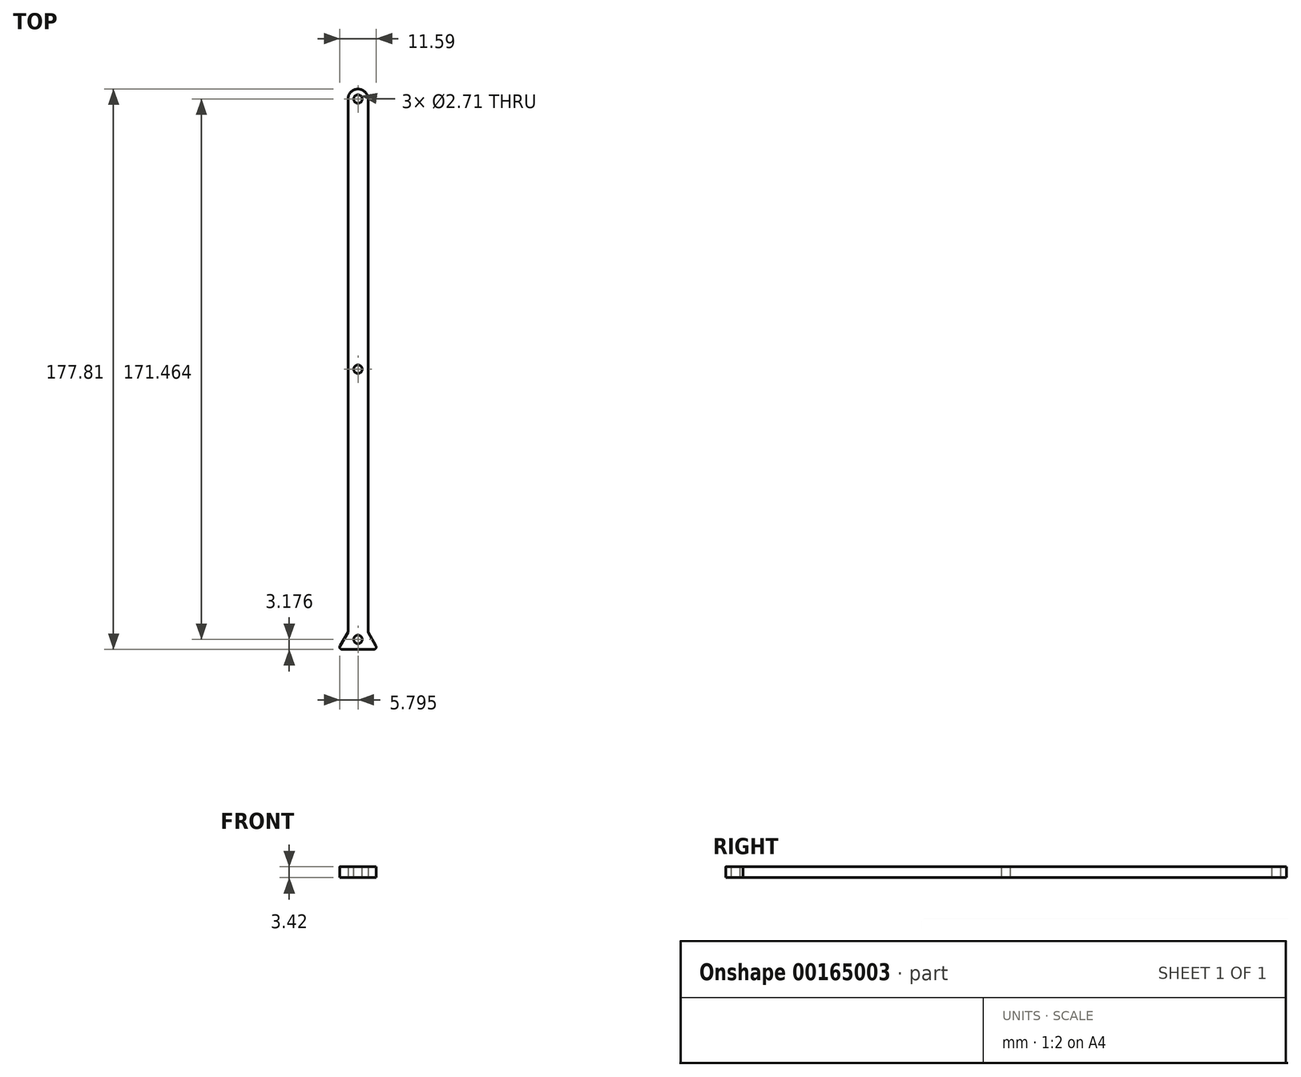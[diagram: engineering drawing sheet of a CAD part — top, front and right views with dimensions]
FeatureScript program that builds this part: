
annotation { "Feature Type Name" : "Feature", "Feature Type Description" : "" }
export const myFeature = defineFeature(function(context is Context, id is Id, definition is map)
    precondition{}
    {
        {
            var Q0;
            Q0=qCreatedBy(makeId("Top.planeOp"),FACE);
            var sketch = newSketch(context, id + "F0", { "sketchPlane" : qUnion([Q0])});
            skLineSegment(sketch, "E0.bottom", {"start": v(0, 0) * mm, "end": v(6.35, 0) * mm, "construction": true});
            skLineSegment(sketch, "E0.top", {"start": v(0, -169.14) * mm, "end": v(6.35, -169.14) * mm, "construction": true});
            skLineSegment(sketch, "E0.left", {"start": v(0, 0) * mm, "end": v(0, -169.14) * mm});
            skLineSegment(sketch, "E0.right", {"start": v(6.35, 0) * mm, "end": v(6.35, -169.14) * mm});
            skArc(sketch, "E1", {"start": v(6.35, 0) * mm, "mid": v(3.18, 3.18) * mm, "end": v(0, 0) * mm});
            skLineSegment(sketch, "E2", {"start": v(6.35, -169.14) * mm, "end": v(9.52, -174.64) * mm});
            skLineSegment(sketch, "E3", {"start": v(9.52, -174.64) * mm, "end": v(-3.17, -174.64) * mm});
            skLineSegment(sketch, "E4", {"start": v(-3.17, -174.64) * mm, "end": v(0, -169.14) * mm});
            skLineSegment(sketch, "E5", {"start": v(3.18, -169.14) * mm, "end": v(3.18, -174.64) * mm, "construction": true});
            skLineSegment(sketch, "E6", {"start": v(6.35, -169.14) * mm, "end": v(6.35, -174.64) * mm, "construction": true});
            skSolve(sketch);
        }
        {
            var Q0;
            Q0 = qSketchRegion(id + "F0", true);
            extrude(context, id + "F1", {"entities" : qUnion([Q0]), "depth" : 3.42 * mm});
        }
        {
            var Q0;
            Q0=makeQuery(id+"F1.opExtrude","SWEPT_EDGE",EDGE,{"disambiguationData":[OSD([sQuery(id+"F0.wireOp",EDGE,"E2"),sQuery(id+"F0.wireOp",EDGE,"E3")])]});
            var Q1;
            Q1=makeQuery(id+"F1.opExtrude","SWEPT_EDGE",EDGE,{"disambiguationData":[OSD([sQuery(id+"F0.wireOp",EDGE,"E3"),sQuery(id+"F0.wireOp",EDGE,"E4")])]});
            fillet(context, id + "F2", {"entities" : qUnion([Q0, Q1]), "radius" : 0.76 * mm, "tangentPropagation" : true, "allowEdgeOverflow" : false});
        }
        {
            var Q0;
            Q0=makeQuery(id+"F1.opExtrude","CAP_FACE",FACE,{"disambiguationData":[OSD([sQuery(id+"F0.wireOp",EDGE,"E0.left"),sQuery(id+"F0.wireOp",EDGE,"E0.right"),sQuery(id+"F0.wireOp",EDGE,"E1"),sQuery(id+"F0.wireOp",EDGE,"E2"),sQuery(id+"F0.wireOp",EDGE,"E3"),sQuery(id+"F0.wireOp",EDGE,"E4")])],"isStart":false});
            var sketch = newSketch(context, id + "F3", { "sketchPlane" : qUnion([Q0])});
            skLineSegment(sketch, "E7", {"start": v(3.18, -174.64) * mm, "end": v(3.18, -171.46) * mm, "construction": true});
            skLineSegment(sketch, "E8", {"start": v(3.18, -171.46) * mm, "end": v(3.18, 0) * mm, "construction": true});
            skCircle(sketch, "E9", {"center": v(3.18, 0) * mm, "radius": 1.35 * mm});
            skCircle(sketch, "E10", {"center": v(3.18, -85.73) * mm, "radius": 1.35 * mm});
            skCircle(sketch, "E11", {"center": v(3.18, -171.46) * mm, "radius": 1.35 * mm});
            skLineSegment(sketch, "E12", {"start": v(3.18, 0) * mm, "end": v(3.18, 3.18) * mm, "construction": true});
            skSolve(sketch);
        }
        {
            var Q0;
            Q0 = qSketchRegion(id + "F3", true);
            var Q1;
            Q1=makeQuery(id+"F1.opExtrude","CAP_FACE",FACE,{"disambiguationData":[OSD([sQuery(id+"F0.wireOp",EDGE,"E0.left"),sQuery(id+"F0.wireOp",EDGE,"E0.right"),sQuery(id+"F0.wireOp",EDGE,"E1"),sQuery(id+"F0.wireOp",EDGE,"E2"),sQuery(id+"F0.wireOp",EDGE,"E3"),sQuery(id+"F0.wireOp",EDGE,"E4")])],"isStart":true});
            extrude(context, id + "F4", {"entities" : qUnion([Q0]), "operationType" : NewBodyOperationType.REMOVE, "endBound" : BoundingType.UP_TO_SURFACE, "oppositeDirection" : true, "endBoundEntityFace" : qUnion([Q1]), "depth" : 25.4 * mm});
        }
    });
